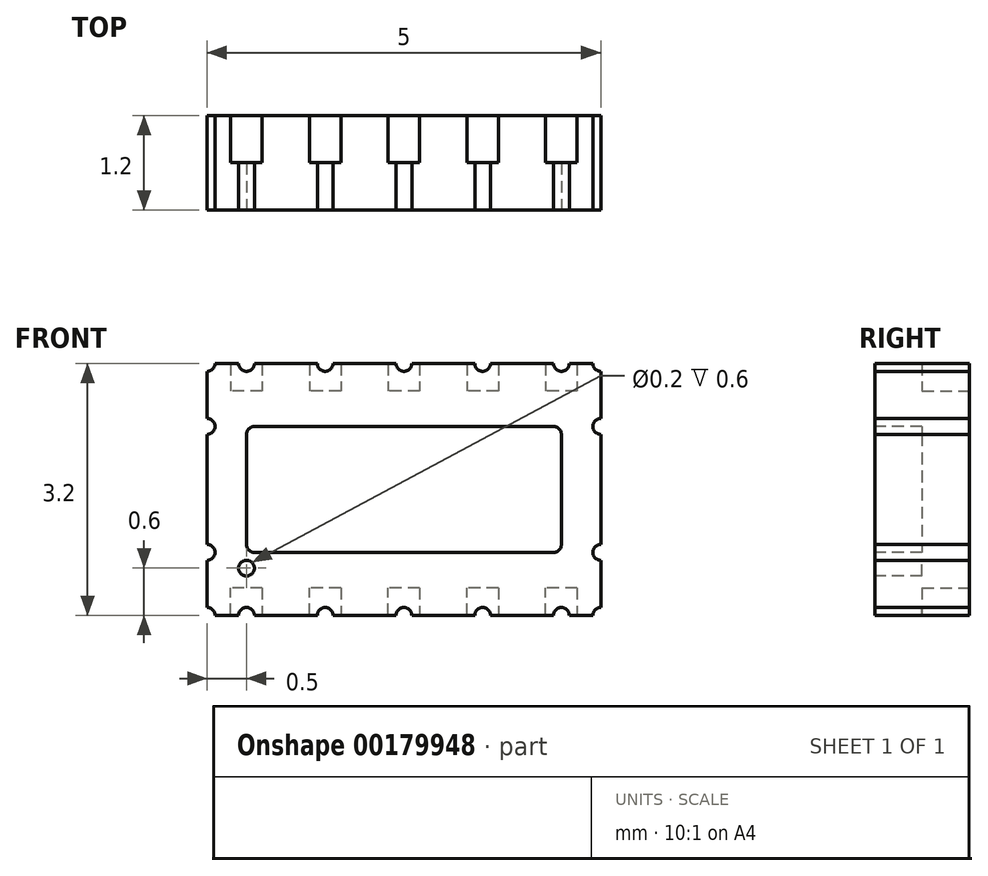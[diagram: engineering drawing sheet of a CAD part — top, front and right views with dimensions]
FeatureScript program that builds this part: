
annotation { "Feature Type Name" : "Feature", "Feature Type Description" : "" }
export const myFeature = defineFeature(function(context is Context, id is Id, definition is map)
    precondition{}
    {
        {
            var Q0;
            Q0=qCreatedBy(makeId("Front.planeOp"),FACE);
            var sketch = newSketch(context, id + "F0", { "sketchPlane" : qUnion([Q0])});
            skLineSegment(sketch, "E0.bottom", {"start": v(-2.4, 1.6) * mm, "end": v(-2.1, 1.6) * mm});
            skLineSegment(sketch, "E0.top", {"start": v(-2.4, -1.6) * mm, "end": v(-2.1, -1.6) * mm});
            skLineSegment(sketch, "E0.left", {"start": v(-2.5, 1.5) * mm, "end": v(-2.5, 0.9) * mm});
            skLineSegment(sketch, "E0.right", {"start": v(2.5, 1.5) * mm, "end": v(2.5, 0.9) * mm});
            skPoint(sketch, "E0.middle", {"position": v(0, 0) * mm});
            skArc(sketch, "E1", {"start": v(2.4, 1.6) * mm, "mid": v(2.43, 1.53) * mm, "end": v(2.5, 1.5) * mm});
            skArc(sketch, "E2", {"start": v(-2.5, 1.5) * mm, "mid": v(-2.43, 1.53) * mm, "end": v(-2.4, 1.6) * mm});
            skArc(sketch, "E3", {"start": v(2.5, -1.5) * mm, "mid": v(2.43, -1.53) * mm, "end": v(2.4, -1.6) * mm});
            skArc(sketch, "E4", {"start": v(-2.4, -1.6) * mm, "mid": v(-2.43, -1.53) * mm, "end": v(-2.5, -1.5) * mm});
            skArc(sketch, "E5", {"start": v(1.9, 1.6) * mm, "mid": v(2, 1.5) * mm, "end": v(2.1, 1.6) * mm});
            skArc(sketch, "E6", {"start": v(0.9, 1.6) * mm, "mid": v(1, 1.5) * mm, "end": v(1.1, 1.6) * mm});
            skArc(sketch, "E7", {"start": v(-0.1, 1.6) * mm, "mid": v(0, 1.5) * mm, "end": v(0.1, 1.6) * mm});
            skArc(sketch, "E8", {"start": v(-1.1, 1.6) * mm, "mid": v(-1, 1.5) * mm, "end": v(-0.9, 1.6) * mm});
            skArc(sketch, "E9", {"start": v(-2.1, 1.6) * mm, "mid": v(-2, 1.5) * mm, "end": v(-1.9, 1.6) * mm});
            skArc(sketch, "E10", {"start": v(-1.9, -1.6) * mm, "mid": v(-2, -1.5) * mm, "end": v(-2.1, -1.6) * mm});
            skArc(sketch, "E11", {"start": v(-0.9, -1.6) * mm, "mid": v(-1, -1.5) * mm, "end": v(-1.1, -1.6) * mm});
            skArc(sketch, "E12", {"start": v(0.1, -1.6) * mm, "mid": v(0, -1.5) * mm, "end": v(-0.1, -1.6) * mm});
            skArc(sketch, "E13", {"start": v(1.1, -1.6) * mm, "mid": v(1, -1.5) * mm, "end": v(0.9, -1.6) * mm});
            skArc(sketch, "E14", {"start": v(2.1, -1.6) * mm, "mid": v(2, -1.5) * mm, "end": v(1.9, -1.6) * mm});
            skArc(sketch, "E15", {"start": v(-2.5, 0.7) * mm, "mid": v(-2.4, 0.8) * mm, "end": v(-2.5, 0.9) * mm});
            skArc(sketch, "E16", {"start": v(-2.5, -0.9) * mm, "mid": v(-2.4, -0.8) * mm, "end": v(-2.5, -0.7) * mm});
            skArc(sketch, "E17", {"start": v(2.5, 0.9) * mm, "mid": v(2.4, 0.8) * mm, "end": v(2.5, 0.7) * mm});
            skArc(sketch, "E18", {"start": v(2.5, -0.7) * mm, "mid": v(2.4, -0.8) * mm, "end": v(2.5, -0.9) * mm});
            skLineSegment(sketch, "E19.trimOffspring", {"start": v(-1.9, 1.6) * mm, "end": v(-1.1, 1.6) * mm});
            skLineSegment(sketch, "E20.trimOffspring", {"start": v(-0.9, 1.6) * mm, "end": v(-0.1, 1.6) * mm});
            skLineSegment(sketch, "E21.trimOffspring", {"start": v(0.1, 1.6) * mm, "end": v(0.9, 1.6) * mm});
            skLineSegment(sketch, "E22.trimOffspring", {"start": v(1.1, 1.6) * mm, "end": v(1.9, 1.6) * mm});
            skLineSegment(sketch, "E23.trimOffspring", {"start": v(2.1, 1.6) * mm, "end": v(2.4, 1.6) * mm});
            skLineSegment(sketch, "E24.trimOffspring", {"start": v(2.5, 0.7) * mm, "end": v(2.5, -0.7) * mm});
            skLineSegment(sketch, "E25.trimOffspring", {"start": v(2.5, -0.9) * mm, "end": v(2.5, -1.5) * mm});
            skLineSegment(sketch, "E26.trimOffspring", {"start": v(2.1, -1.6) * mm, "end": v(2.4, -1.6) * mm});
            skLineSegment(sketch, "E27.trimOffspring", {"start": v(1.1, -1.6) * mm, "end": v(1.9, -1.6) * mm});
            skLineSegment(sketch, "E28.trimOffspring", {"start": v(0.1, -1.6) * mm, "end": v(0.9, -1.6) * mm});
            skLineSegment(sketch, "E29.trimOffspring", {"start": v(-0.9, -1.6) * mm, "end": v(-0.1, -1.6) * mm});
            skLineSegment(sketch, "E30.trimOffspring", {"start": v(-1.9, -1.6) * mm, "end": v(-1.1, -1.6) * mm});
            skLineSegment(sketch, "E31.trimOffspring", {"start": v(-2.5, -0.9) * mm, "end": v(-2.5, -1.5) * mm});
            skLineSegment(sketch, "E32.trimOffspring", {"start": v(-2.5, 0.7) * mm, "end": v(-2.5, -0.7) * mm});
            skSolve(sketch);
        }
        {
            var Q0;
            Q0=makeQuery(id+"F0.imprint","IMPRINT",FACE,{"disambiguationData":[TD([[makeQuery(id+"F0.imprint","IMPRINT",EDGE,{"derivedFrom":sQuery(id+"F0.wireOp",EDGE,"E0.bottom")}),-1.0]])]});
            extrude(context, id + "F1", {"entities" : qUnion([Q0]), "depth" : 1.2 * mm});
        }
        {
            var Q0;
            Q0=makeQuery(id+"F1.opExtrude","CAP_FACE",FACE,{"disambiguationData":[OSD([sQuery(id+"F0.wireOp",EDGE,"E0.bottom"),sQuery(id+"F0.wireOp",EDGE,"E0.top"),sQuery(id+"F0.wireOp",EDGE,"E0.left"),sQuery(id+"F0.wireOp",EDGE,"E0.right"),sQuery(id+"F0.wireOp",EDGE,"E1"),sQuery(id+"F0.wireOp",EDGE,"E2"),sQuery(id+"F0.wireOp",EDGE,"E3"),sQuery(id+"F0.wireOp",EDGE,"E4"),sQuery(id+"F0.wireOp",EDGE,"E5"),sQuery(id+"F0.wireOp",EDGE,"E6"),sQuery(id+"F0.wireOp",EDGE,"E7"),sQuery(id+"F0.wireOp",EDGE,"E8"),sQuery(id+"F0.wireOp",EDGE,"E9"),sQuery(id+"F0.wireOp",EDGE,"E10"),sQuery(id+"F0.wireOp",EDGE,"E11"),sQuery(id+"F0.wireOp",EDGE,"E12"),sQuery(id+"F0.wireOp",EDGE,"E13"),sQuery(id+"F0.wireOp",EDGE,"E14"),sQuery(id+"F0.wireOp",EDGE,"E15"),sQuery(id+"F0.wireOp",EDGE,"E16"),sQuery(id+"F0.wireOp",EDGE,"E17"),sQuery(id+"F0.wireOp",EDGE,"E18"),sQuery(id+"F0.wireOp",EDGE,"E19.trimOffspring"),sQuery(id+"F0.wireOp",EDGE,"E20.trimOffspring"),sQuery(id+"F0.wireOp",EDGE,"E21.trimOffspring"),sQuery(id+"F0.wireOp",EDGE,"E22.trimOffspring"),sQuery(id+"F0.wireOp",EDGE,"E23.trimOffspring"),sQuery(id+"F0.wireOp",EDGE,"E24.trimOffspring"),sQuery(id+"F0.wireOp",EDGE,"E25.trimOffspring"),sQuery(id+"F0.wireOp",EDGE,"E26.trimOffspring"),sQuery(id+"F0.wireOp",EDGE,"E27.trimOffspring"),sQuery(id+"F0.wireOp",EDGE,"E28.trimOffspring"),sQuery(id+"F0.wireOp",EDGE,"E29.trimOffspring"),sQuery(id+"F0.wireOp",EDGE,"E30.trimOffspring"),sQuery(id+"F0.wireOp",EDGE,"E31.trimOffspring"),sQuery(id+"F0.wireOp",EDGE,"E32.trimOffspring")])],"isStart":false});
            var sketch = newSketch(context, id + "F2", { "sketchPlane" : qUnion([Q0])});
            skCircle(sketch, "E33", {"center": v(-2, -1) * mm, "radius": 0.1 * mm});
            skSolve(sketch);
        }
        {
            var Q0;
            Q0 = qSketchRegion(id + "F2", true);
            extrude(context, id + "F3", {"entities" : qUnion([Q0]), "operationType" : NewBodyOperationType.REMOVE, "oppositeDirection" : true, "depth" : 0.6 * mm});
        }
        {
            var Q0;
            Q0=makeQuery(id+"F1.opExtrude","CAP_FACE",FACE,{"disambiguationData":[OSD([sQuery(id+"F0.wireOp",EDGE,"E0.bottom"),sQuery(id+"F0.wireOp",EDGE,"E0.top"),sQuery(id+"F0.wireOp",EDGE,"E0.left"),sQuery(id+"F0.wireOp",EDGE,"E0.right"),sQuery(id+"F0.wireOp",EDGE,"E1"),sQuery(id+"F0.wireOp",EDGE,"E2"),sQuery(id+"F0.wireOp",EDGE,"E3"),sQuery(id+"F0.wireOp",EDGE,"E4"),sQuery(id+"F0.wireOp",EDGE,"E5"),sQuery(id+"F0.wireOp",EDGE,"E6"),sQuery(id+"F0.wireOp",EDGE,"E7"),sQuery(id+"F0.wireOp",EDGE,"E8"),sQuery(id+"F0.wireOp",EDGE,"E9"),sQuery(id+"F0.wireOp",EDGE,"E10"),sQuery(id+"F0.wireOp",EDGE,"E11"),sQuery(id+"F0.wireOp",EDGE,"E12"),sQuery(id+"F0.wireOp",EDGE,"E13"),sQuery(id+"F0.wireOp",EDGE,"E14"),sQuery(id+"F0.wireOp",EDGE,"E15"),sQuery(id+"F0.wireOp",EDGE,"E16"),sQuery(id+"F0.wireOp",EDGE,"E17"),sQuery(id+"F0.wireOp",EDGE,"E18"),sQuery(id+"F0.wireOp",EDGE,"E19.trimOffspring"),sQuery(id+"F0.wireOp",EDGE,"E20.trimOffspring"),sQuery(id+"F0.wireOp",EDGE,"E21.trimOffspring"),sQuery(id+"F0.wireOp",EDGE,"E22.trimOffspring"),sQuery(id+"F0.wireOp",EDGE,"E23.trimOffspring"),sQuery(id+"F0.wireOp",EDGE,"E24.trimOffspring"),sQuery(id+"F0.wireOp",EDGE,"E25.trimOffspring"),sQuery(id+"F0.wireOp",EDGE,"E26.trimOffspring"),sQuery(id+"F0.wireOp",EDGE,"E27.trimOffspring"),sQuery(id+"F0.wireOp",EDGE,"E28.trimOffspring"),sQuery(id+"F0.wireOp",EDGE,"E29.trimOffspring"),sQuery(id+"F0.wireOp",EDGE,"E30.trimOffspring"),sQuery(id+"F0.wireOp",EDGE,"E31.trimOffspring"),sQuery(id+"F0.wireOp",EDGE,"E32.trimOffspring")])],"isStart":false});
            var sketch = newSketch(context, id + "F4", { "sketchPlane" : qUnion([Q0])});
            skLineSegment(sketch, "E34.bottom", {"start": v(-2, 0.8) * mm, "end": v(2, 0.8) * mm});
            skLineSegment(sketch, "E34.top", {"start": v(-2, -0.8) * mm, "end": v(2, -0.8) * mm});
            skLineSegment(sketch, "E34.left", {"start": v(-2, 0.8) * mm, "end": v(-2, -0.8) * mm});
            skLineSegment(sketch, "E34.right", {"start": v(2, 0.8) * mm, "end": v(2, -0.8) * mm});
            skPoint(sketch, "E34.middle", {"position": v(0, 0) * mm});
            skSolve(sketch);
        }
        {
            var Q0;
            Q0=makeQuery(id+"F4.imprint","IMPRINT",FACE,{"disambiguationData":[TD([[makeQuery(id+"F4.imprint","IMPRINT",EDGE,{"derivedFrom":sQuery(id+"F4.wireOp",EDGE,"E34.bottom")}),-1.0]])]});
            extrude(context, id + "F5", {"entities" : qUnion([Q0]), "operationType" : NewBodyOperationType.REMOVE, "oppositeDirection" : true, "depth" : 0.6 * mm});
        }
        {
            var Q0;
            Q0=makeQuery(id+"F5.boolean.opBoolean","COPY",EDGE,{"derivedFrom":makeQuery(id+"F5.opExtrude","SWEPT_EDGE",EDGE,{"disambiguationData":[OSD([sQuery(id+"F4.wireOp",EDGE,"E34.top"),sQuery(id+"F4.wireOp",EDGE,"E34.left")])]})});
            var Q1;
            Q1=makeQuery(id+"F5.boolean.opBoolean","COPY",EDGE,{"derivedFrom":makeQuery(id+"F5.opExtrude","SWEPT_EDGE",EDGE,{"disambiguationData":[OSD([sQuery(id+"F4.wireOp",EDGE,"E34.bottom"),sQuery(id+"F4.wireOp",EDGE,"E34.right")])]})});
            var Q2;
            Q2=makeQuery(id+"F5.boolean.opBoolean","COPY",EDGE,{"derivedFrom":makeQuery(id+"F5.opExtrude","SWEPT_EDGE",EDGE,{"disambiguationData":[OSD([sQuery(id+"F4.wireOp",EDGE,"E34.top"),sQuery(id+"F4.wireOp",EDGE,"E34.right")])]})});
            var Q3;
            Q3=makeQuery(id+"F5.boolean.opBoolean","COPY",EDGE,{"derivedFrom":makeQuery(id+"F5.opExtrude","SWEPT_EDGE",EDGE,{"disambiguationData":[OSD([sQuery(id+"F4.wireOp",EDGE,"E34.bottom"),sQuery(id+"F4.wireOp",EDGE,"E34.left")])]})});
            fillet(context, id + "F6", {"entities" : qUnion([Q0, Q1, Q2, Q3]), "radius" : 0.1 * mm, "tangentPropagation" : true, "allowEdgeOverflow" : false});
        }
        {
            var Q0;
            Q0=makeQuery(id+"F1.opExtrude","CAP_FACE",FACE,{"disambiguationData":[OSD([sQuery(id+"F0.wireOp",EDGE,"E0.bottom"),sQuery(id+"F0.wireOp",EDGE,"E0.top"),sQuery(id+"F0.wireOp",EDGE,"E0.left"),sQuery(id+"F0.wireOp",EDGE,"E0.right"),sQuery(id+"F0.wireOp",EDGE,"E1"),sQuery(id+"F0.wireOp",EDGE,"E2"),sQuery(id+"F0.wireOp",EDGE,"E3"),sQuery(id+"F0.wireOp",EDGE,"E4"),sQuery(id+"F0.wireOp",EDGE,"E5"),sQuery(id+"F0.wireOp",EDGE,"E6"),sQuery(id+"F0.wireOp",EDGE,"E7"),sQuery(id+"F0.wireOp",EDGE,"E8"),sQuery(id+"F0.wireOp",EDGE,"E9"),sQuery(id+"F0.wireOp",EDGE,"E10"),sQuery(id+"F0.wireOp",EDGE,"E11"),sQuery(id+"F0.wireOp",EDGE,"E12"),sQuery(id+"F0.wireOp",EDGE,"E13"),sQuery(id+"F0.wireOp",EDGE,"E14"),sQuery(id+"F0.wireOp",EDGE,"E15"),sQuery(id+"F0.wireOp",EDGE,"E16"),sQuery(id+"F0.wireOp",EDGE,"E17"),sQuery(id+"F0.wireOp",EDGE,"E18"),sQuery(id+"F0.wireOp",EDGE,"E19.trimOffspring"),sQuery(id+"F0.wireOp",EDGE,"E20.trimOffspring"),sQuery(id+"F0.wireOp",EDGE,"E21.trimOffspring"),sQuery(id+"F0.wireOp",EDGE,"E22.trimOffspring"),sQuery(id+"F0.wireOp",EDGE,"E23.trimOffspring"),sQuery(id+"F0.wireOp",EDGE,"E24.trimOffspring"),sQuery(id+"F0.wireOp",EDGE,"E25.trimOffspring"),sQuery(id+"F0.wireOp",EDGE,"E26.trimOffspring"),sQuery(id+"F0.wireOp",EDGE,"E27.trimOffspring"),sQuery(id+"F0.wireOp",EDGE,"E28.trimOffspring"),sQuery(id+"F0.wireOp",EDGE,"E29.trimOffspring"),sQuery(id+"F0.wireOp",EDGE,"E30.trimOffspring"),sQuery(id+"F0.wireOp",EDGE,"E31.trimOffspring"),sQuery(id+"F0.wireOp",EDGE,"E32.trimOffspring")])],"isStart":true});
            var sketch = newSketch(context, id + "F7", { "sketchPlane" : qUnion([Q0])});
            skLineSegment(sketch, "E35", {"start": v(-0.2, 2.23) * mm, "end": v(-0.2, -2.15) * mm});
            skLineSegment(sketch, "E36", {"start": v(-1.2, 2.44) * mm, "end": v(-1.2, -2.13) * mm});
            skLineSegment(sketch, "E37", {"start": v(-2.2, 2.43) * mm, "end": v(-2.2, -2.19) * mm});
            skLineSegment(sketch, "E38", {"start": v(0.8, 2.27) * mm, "end": v(0.8, -2.13) * mm});
            skLineSegment(sketch, "E39", {"start": v(1.8, 2.28) * mm, "end": v(1.8, -2.18) * mm});
            skLineSegment(sketch, "E40.bottom", {"start": v(-2.2, 1.6) * mm, "end": v(-1.8, 1.6) * mm});
            skLineSegment(sketch, "E40.top", {"start": v(-2.2, 1.25) * mm, "end": v(-1.8, 1.25) * mm});
            skLineSegment(sketch, "E40.left", {"start": v(-2.2, 1.6) * mm, "end": v(-2.2, 1.25) * mm});
            skLineSegment(sketch, "E40.right", {"start": v(-1.8, 1.6) * mm, "end": v(-1.8, 1.25) * mm});
            skLineSegment(sketch, "E41.bottom", {"start": v(-1.2, 1.6) * mm, "end": v(-0.8, 1.6) * mm});
            skLineSegment(sketch, "E41.top", {"start": v(-1.2, 1.25) * mm, "end": v(-0.8, 1.25) * mm});
            skLineSegment(sketch, "E41.left", {"start": v(-1.2, 1.6) * mm, "end": v(-1.2, 1.25) * mm});
            skLineSegment(sketch, "E41.right", {"start": v(-0.8, 1.6) * mm, "end": v(-0.8, 1.25) * mm});
            skLineSegment(sketch, "E42.bottom", {"start": v(-0.2, 1.6) * mm, "end": v(0.2, 1.6) * mm});
            skLineSegment(sketch, "E42.top", {"start": v(-0.2, 1.25) * mm, "end": v(0.2, 1.25) * mm});
            skLineSegment(sketch, "E42.left", {"start": v(-0.2, 1.6) * mm, "end": v(-0.2, 1.25) * mm});
            skLineSegment(sketch, "E42.right", {"start": v(0.2, 1.6) * mm, "end": v(0.2, 1.25) * mm});
            skLineSegment(sketch, "E43.bottom", {"start": v(0.8, 1.6) * mm, "end": v(1.2, 1.6) * mm});
            skLineSegment(sketch, "E43.top", {"start": v(0.8, 1.25) * mm, "end": v(1.2, 1.25) * mm});
            skLineSegment(sketch, "E43.left", {"start": v(0.8, 1.6) * mm, "end": v(0.8, 1.25) * mm});
            skLineSegment(sketch, "E43.right", {"start": v(1.2, 1.6) * mm, "end": v(1.2, 1.25) * mm});
            skLineSegment(sketch, "E44.bottom", {"start": v(1.8, 1.6) * mm, "end": v(2.2, 1.6) * mm});
            skLineSegment(sketch, "E44.top", {"start": v(1.8, 1.25) * mm, "end": v(2.2, 1.25) * mm});
            skLineSegment(sketch, "E44.left", {"start": v(1.8, 1.6) * mm, "end": v(1.8, 1.25) * mm});
            skLineSegment(sketch, "E44.right", {"start": v(2.2, 1.6) * mm, "end": v(2.2, 1.25) * mm});
            skLineSegment(sketch, "E45.bottom", {"start": v(-2.2, -1.6) * mm, "end": v(-1.8, -1.6) * mm});
            skLineSegment(sketch, "E45.top", {"start": v(-2.2, -1.25) * mm, "end": v(-1.8, -1.25) * mm});
            skLineSegment(sketch, "E45.left", {"start": v(-2.2, -1.6) * mm, "end": v(-2.2, -1.25) * mm});
            skLineSegment(sketch, "E45.right", {"start": v(-1.8, -1.6) * mm, "end": v(-1.8, -1.25) * mm});
            skLineSegment(sketch, "E46.bottom", {"start": v(-1.2, -1.6) * mm, "end": v(-0.8, -1.6) * mm});
            skLineSegment(sketch, "E46.top", {"start": v(-1.2, -1.25) * mm, "end": v(-0.8, -1.25) * mm});
            skLineSegment(sketch, "E46.left", {"start": v(-1.2, -1.6) * mm, "end": v(-1.2, -1.25) * mm});
            skLineSegment(sketch, "E46.right", {"start": v(-0.8, -1.6) * mm, "end": v(-0.8, -1.25) * mm});
            skLineSegment(sketch, "E47.bottom", {"start": v(-0.2, -1.6) * mm, "end": v(0.2, -1.6) * mm});
            skLineSegment(sketch, "E47.top", {"start": v(-0.2, -1.25) * mm, "end": v(0.2, -1.25) * mm});
            skLineSegment(sketch, "E47.left", {"start": v(-0.2, -1.6) * mm, "end": v(-0.2, -1.25) * mm});
            skLineSegment(sketch, "E47.right", {"start": v(0.2, -1.6) * mm, "end": v(0.2, -1.25) * mm});
            skLineSegment(sketch, "E48.bottom", {"start": v(0.8, -1.6) * mm, "end": v(1.2, -1.6) * mm});
            skLineSegment(sketch, "E48.top", {"start": v(0.8, -1.25) * mm, "end": v(1.2, -1.25) * mm});
            skLineSegment(sketch, "E48.left", {"start": v(0.8, -1.6) * mm, "end": v(0.8, -1.25) * mm});
            skLineSegment(sketch, "E48.right", {"start": v(1.2, -1.6) * mm, "end": v(1.2, -1.25) * mm});
            skLineSegment(sketch, "E49.bottom", {"start": v(1.8, -1.6) * mm, "end": v(2.2, -1.6) * mm});
            skLineSegment(sketch, "E49.top", {"start": v(1.8, -1.25) * mm, "end": v(2.2, -1.25) * mm});
            skLineSegment(sketch, "E49.left", {"start": v(1.8, -1.6) * mm, "end": v(1.8, -1.25) * mm});
            skLineSegment(sketch, "E49.right", {"start": v(2.2, -1.6) * mm, "end": v(2.2, -1.25) * mm});
            skSolve(sketch);
        }
        {
            var Q0;
            Q0=makeQuery(id+"F7.imprint","IMPRINT",FACE,{"disambiguationData":[TD([[makeQuery(id+"F7.imprint","IMPRINT",EDGE,{"derivedFrom":sQuery(id+"F7.wireOp",EDGE,"E40.top")}),1.0]])]});
            var Q1;
            Q1=makeQuery(id+"F7.imprint","IMPRINT",FACE,{"disambiguationData":[TD([[makeQuery(id+"F7.imprint","IMPRINT",EDGE,{"derivedFrom":sQuery(id+"F7.wireOp",EDGE,"E41.top")}),1.0]])]});
            var Q2;
            Q2=makeQuery(id+"F7.imprint","IMPRINT",FACE,{"disambiguationData":[TD([[makeQuery(id+"F7.imprint","IMPRINT",EDGE,{"derivedFrom":sQuery(id+"F7.wireOp",EDGE,"E42.top")}),1.0]])]});
            var Q3;
            Q3=makeQuery(id+"F7.imprint","IMPRINT",FACE,{"disambiguationData":[TD([[makeQuery(id+"F7.imprint","IMPRINT",EDGE,{"derivedFrom":sQuery(id+"F7.wireOp",EDGE,"E43.top")}),1.0]])]});
            var Q4;
            Q4=makeQuery(id+"F7.imprint","IMPRINT",FACE,{"disambiguationData":[TD([[makeQuery(id+"F7.imprint","IMPRINT",EDGE,{"derivedFrom":sQuery(id+"F7.wireOp",EDGE,"E44.top")}),1.0]])]});
            var Q5;
            Q5=makeQuery(id+"F7.imprint","IMPRINT",FACE,{"disambiguationData":[TD([[makeQuery(id+"F7.imprint","IMPRINT",EDGE,{"derivedFrom":sQuery(id+"F7.wireOp",EDGE,"E49.top")}),-1.0]])]});
            var Q6;
            Q6=makeQuery(id+"F7.imprint","IMPRINT",FACE,{"disambiguationData":[TD([[makeQuery(id+"F7.imprint","IMPRINT",EDGE,{"derivedFrom":sQuery(id+"F7.wireOp",EDGE,"E48.top")}),-1.0]])]});
            var Q7;
            Q7=makeQuery(id+"F7.imprint","IMPRINT",FACE,{"disambiguationData":[TD([[makeQuery(id+"F7.imprint","IMPRINT",EDGE,{"derivedFrom":sQuery(id+"F7.wireOp",EDGE,"E47.top")}),-1.0]])]});
            var Q8;
            Q8=makeQuery(id+"F7.imprint","IMPRINT",FACE,{"disambiguationData":[TD([[makeQuery(id+"F7.imprint","IMPRINT",EDGE,{"derivedFrom":sQuery(id+"F7.wireOp",EDGE,"E46.top")}),-1.0]])]});
            var Q9;
            Q9=makeQuery(id+"F7.imprint","IMPRINT",FACE,{"disambiguationData":[TD([[makeQuery(id+"F7.imprint","IMPRINT",EDGE,{"derivedFrom":sQuery(id+"F7.wireOp",EDGE,"E45.top")}),-1.0]])]});
            extrude(context, id + "F8", {"entities" : qUnion([Q0, Q1, Q2, Q3, Q4, Q5, Q6, Q7, Q8, Q9]), "operationType" : NewBodyOperationType.REMOVE, "oppositeDirection" : true, "depth" : 0.6 * mm});
        }
    });
